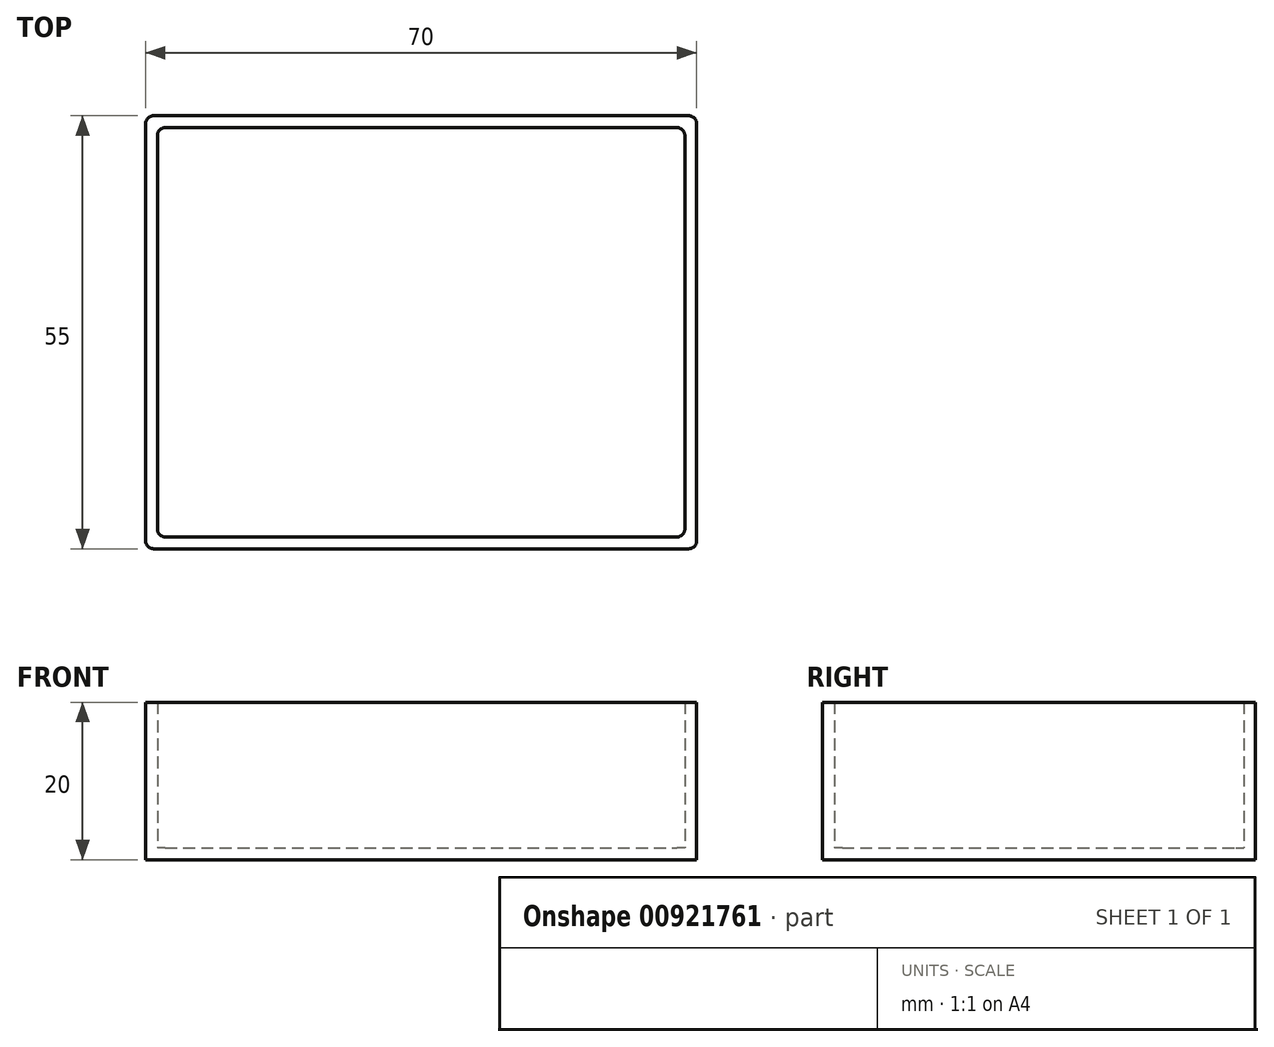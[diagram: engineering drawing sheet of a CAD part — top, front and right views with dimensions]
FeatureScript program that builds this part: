
annotation { "Feature Type Name" : "Feature", "Feature Type Description" : "" }
export const myFeature = defineFeature(function(context is Context, id is Id, definition is map)
    precondition{}
    {
        {
            var Q0;
            Q0=qCreatedBy(makeId("Top.planeOp"),FACE);
            var sketch = newSketch(context, id + "F0", { "sketchPlane" : qUnion([Q0])});
            skLineSegment(sketch, "E0.bottom", {"start": v(0, 0) * mm, "end": v(70, 0) * mm});
            skLineSegment(sketch, "E0.top", {"start": v(0, 55) * mm, "end": v(70, 55) * mm});
            skLineSegment(sketch, "E0.left", {"start": v(0, 0) * mm, "end": v(0, 55) * mm});
            skLineSegment(sketch, "E0.right", {"start": v(70, 0) * mm, "end": v(70, 55) * mm});
            skSolve(sketch);
        }
        {
            var Q0;
            Q0=makeQuery(id+"F0.imprint","IMPRINT",FACE,{"disambiguationData":[TD([[makeQuery(id+"F0.imprint","IMPRINT",EDGE,{"derivedFrom":sQuery(id+"F0.wireOp",EDGE,"E0.bottom")}),1.0]])]});
            extrude(context, id + "F1", {"entities" : qUnion([Q0]), "depth" : 20 * mm, "offsetDistance" : 25 * mm});
        }
        {
            var Q0;
            Q0=makeQuery(id+"F1.opExtrude","CAP_FACE",FACE,{"disambiguationData":[OSD([sQuery(id+"F0.wireOp",EDGE,"E0.bottom"),sQuery(id+"F0.wireOp",EDGE,"E0.top"),sQuery(id+"F0.wireOp",EDGE,"E0.left"),sQuery(id+"F0.wireOp",EDGE,"E0.right")])],"isStart":false});
            shell(context, id + "F2", {"entities" : qUnion([Q0]), "thickness" : 1.5 * mm});
        }
        {
            var Q0;
            Q0=makeQuery(id+"F1.opExtrude","SWEPT_EDGE",EDGE,{"disambiguationData":[OSD([sQuery(id+"F0.wireOp",EDGE,"E0.top"),sQuery(id+"F0.wireOp",EDGE,"E0.left")])]});
            var Q1;
            Q1=makeQuery(id+"F2.opShell","OFFSET_EDGE",EDGE,{"disambiguationData":[OSD([sQuery(id+"F0.wireOp",EDGE,"E0.top"),sQuery(id+"F0.wireOp",EDGE,"E0.left")])]});
            fillet(context, id + "F3", {"entities" : qUnion([Q0, Q1]), "radius" : 1 * mm, "tangentPropagation" : true, "allowEdgeOverflow" : false});
        }
        {
            var Q0;
            Q0=makeQuery(id+"F1.opExtrude","SWEPT_EDGE",EDGE,{"disambiguationData":[OSD([sQuery(id+"F0.wireOp",EDGE,"E0.bottom"),sQuery(id+"F0.wireOp",EDGE,"E0.left")])]});
            fillet(context, id + "F4", {"entities" : qUnion([Q0]), "radius" : 1 * mm, "tangentPropagation" : true, "allowEdgeOverflow" : false});
        }
        {
            var Q0;
            Q0=makeQuery(id+"F1.opExtrude","SWEPT_EDGE",EDGE,{"disambiguationData":[OSD([sQuery(id+"F0.wireOp",EDGE,"E0.bottom"),sQuery(id+"F0.wireOp",EDGE,"E0.right")])]});
            fillet(context, id + "F5", {"entities" : qUnion([Q0]), "radius" : 1 * mm, "tangentPropagation" : true, "allowEdgeOverflow" : false});
        }
        {
            var Q0;
            Q0=makeQuery(id+"F1.opExtrude","SWEPT_EDGE",EDGE,{"disambiguationData":[OSD([sQuery(id+"F0.wireOp",EDGE,"E0.top"),sQuery(id+"F0.wireOp",EDGE,"E0.right")])]});
            fillet(context, id + "F6", {"entities" : qUnion([Q0]), "radius" : 1 * mm, "tangentPropagation" : true, "allowEdgeOverflow" : false});
        }
        {
            var Q0;
            Q0=makeQuery(id+"F2.opShell","OFFSET_EDGE",EDGE,{"disambiguationData":[OSD([sQuery(id+"F0.wireOp",EDGE,"E0.bottom"),sQuery(id+"F0.wireOp",EDGE,"E0.right")])]});
            fillet(context, id + "F7", {"entities" : qUnion([Q0]), "radius" : 1 * mm, "tangentPropagation" : true, "allowEdgeOverflow" : false});
        }
        {
            var Q0;
            Q0=makeQuery(id+"F2.opShell","OFFSET_EDGE",EDGE,{"disambiguationData":[OSD([sQuery(id+"F0.wireOp",EDGE,"E0.bottom"),sQuery(id+"F0.wireOp",EDGE,"E0.left")])]});
            fillet(context, id + "F8", {"entities" : qUnion([Q0]), "radius" : 1 * mm, "tangentPropagation" : true, "allowEdgeOverflow" : false});
        }
        {
            var Q0;
            Q0=makeQuery(id+"F2.opShell","OFFSET_EDGE",EDGE,{"disambiguationData":[OSD([sQuery(id+"F0.wireOp",EDGE,"E0.top"),sQuery(id+"F0.wireOp",EDGE,"E0.right")])]});
            fillet(context, id + "F9", {"entities" : qUnion([Q0]), "radius" : 1 * mm, "tangentPropagation" : true, "allowEdgeOverflow" : false});
        }
    });
